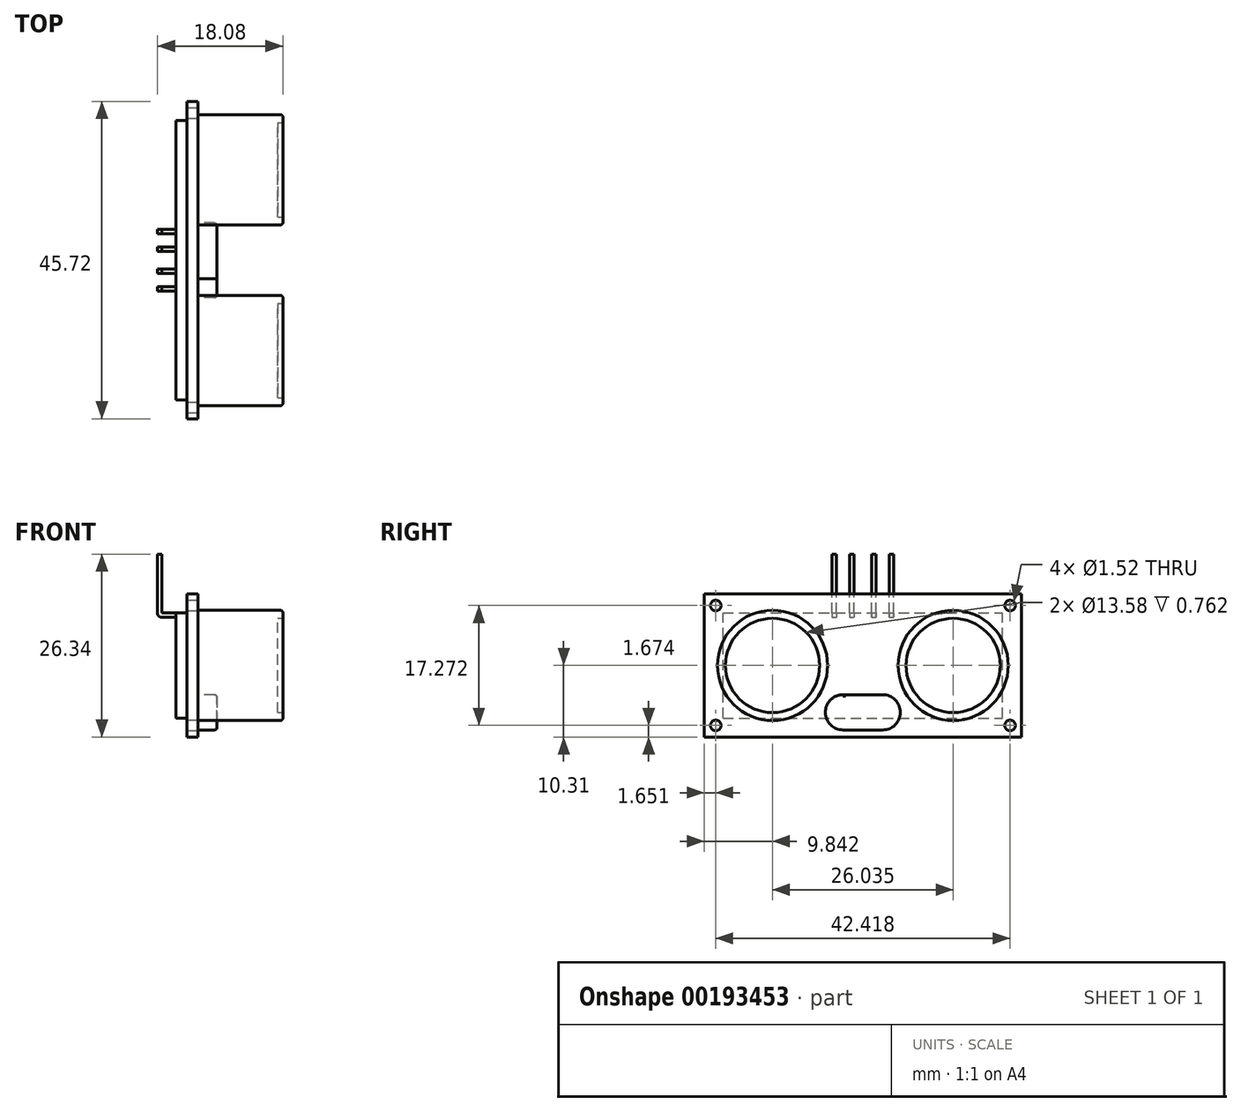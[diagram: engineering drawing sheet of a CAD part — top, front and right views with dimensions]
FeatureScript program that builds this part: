
annotation { "Feature Type Name" : "Feature", "Feature Type Description" : "" }
export const myFeature = defineFeature(function(context is Context, id is Id, definition is map)
    precondition{}
    {
        {
            var Q0;
            Q0=qCreatedBy(makeId("Right.planeOp"),FACE);
            var sketch = newSketch(context, id + "F0", { "sketchPlane" : qUnion([Q0])});
            skLineSegment(sketch, "E0.bottom", {"start": v(22.86, -10.31) * mm, "end": v(-22.86, -10.31) * mm});
            skLineSegment(sketch, "E0.top", {"start": v(22.86, 10.31) * mm, "end": v(-22.86, 10.31) * mm});
            skLineSegment(sketch, "E0.left", {"start": v(22.86, -10.31) * mm, "end": v(22.86, 10.31) * mm});
            skLineSegment(sketch, "E0.right", {"start": v(-22.86, -10.31) * mm, "end": v(-22.86, 10.31) * mm});
            skPoint(sketch, "E0.middle", {"position": v(0, 0) * mm});
            skSolve(sketch);
        }
        {
            var Q0;
            Q0=makeQuery(id+"F0.imprint","IMPRINT",FACE,{"disambiguationData":[TD([[makeQuery(id+"F0.imprint","IMPRINT",EDGE,{"derivedFrom":sQuery(id+"F0.wireOp",EDGE,"E0.bottom")}),-1.0]])]});
            extrude(context, id + "F1", {"entities" : qUnion([Q0]), "oppositeDirection" : true, "depth" : 3.17 * mm});
        }
        {
            var Q0;
            Q0=makeQuery(id+"F1.opExtrude","CAP_FACE",FACE,{"disambiguationData":[OSD([sQuery(id+"F0.wireOp",EDGE,"E0.bottom"),sQuery(id+"F0.wireOp",EDGE,"E0.top"),sQuery(id+"F0.wireOp",EDGE,"E0.left"),sQuery(id+"F0.wireOp",EDGE,"E0.right")])],"isStart":true});
            var sketch = newSketch(context, id + "F2", { "sketchPlane" : qUnion([Q0])});
            skLineSegment(sketch, "E1", {"start": v(0, 0) * mm, "end": v(19.75, 0) * mm, "construction": true});
            skLineSegment(sketch, "E2", {"start": v(0, 0) * mm, "end": v(0, -13.51) * mm, "construction": true});
            skCircle(sketch, "E3", {"center": v(-13.02, 0) * mm, "radius": 7.94 * mm});
            skCircle(sketch, "E4.MirrorC", {"center": v(13.02, 0) * mm, "radius": 7.94 * mm});
            skSolve(sketch);
        }
        {
            var Q0;
            Q0 = qSketchRegion(id + "F2", true);
            extrude(context, id + "F3", {"entities" : qUnion([Q0]), "operationType" : NewBodyOperationType.ADD, "depth" : 12.24 * mm});
        }
        {
            var Q0;
            Q0=makeQuery(id+"F1.opExtrude","CAP_FACE",FACE,{"disambiguationData":[OSD([sQuery(id+"F0.wireOp",EDGE,"E0.bottom"),sQuery(id+"F0.wireOp",EDGE,"E0.top"),sQuery(id+"F0.wireOp",EDGE,"E0.left"),sQuery(id+"F0.wireOp",EDGE,"E0.right")])],"isStart":true});
            var sketch = newSketch(context, id + "F4", { "sketchPlane" : qUnion([Q0])});
            skLineSegment(sketch, "E5", {"start": v(0, 0) * mm, "end": v(0, -8.96) * mm, "construction": true});
            skLineSegment(sketch, "E6", {"start": v(0, 0) * mm, "end": v(11, 0) * mm, "construction": true});
            skCircle(sketch, "E7", {"center": v(-21.2, 8.64) * mm, "radius": 0.76 * mm});
            skCircle(sketch, "E8.MirrorC", {"center": v(21.2, 8.64) * mm, "radius": 0.76 * mm});
            skCircle(sketch, "E9.MirrorC", {"center": v(-21.2, -8.64) * mm, "radius": 0.76 * mm});
            skCircle(sketch, "E10.MirrorC", {"center": v(21.2, -8.64) * mm, "radius": 0.76 * mm});
            skSolve(sketch);
        }
        {
            var Q0;
            Q0 = qSketchRegion(id + "F4", true);
            extrude(context, id + "F5", {"entities" : qUnion([Q0]), "operationType" : NewBodyOperationType.REMOVE, "oppositeDirection" : true, "depth" : 25.4 * mm});
        }
        {
            var Q0;
            Q0=makeQuery(id+"F1.opExtrude","CAP_FACE",FACE,{"disambiguationData":[OSD([sQuery(id+"F0.wireOp",EDGE,"E0.bottom"),sQuery(id+"F0.wireOp",EDGE,"E0.top"),sQuery(id+"F0.wireOp",EDGE,"E0.left"),sQuery(id+"F0.wireOp",EDGE,"E0.right")])],"isStart":false});
            var sketch = newSketch(context, id + "F6", { "sketchPlane" : qUnion([Q0])});
            skLineSegment(sketch, "E11.bottom", {"start": v(20.15, -7.6) * mm, "end": v(-20.15, -7.6) * mm});
            skLineSegment(sketch, "E11.top", {"start": v(20.15, 7.6) * mm, "end": v(-20.15, 7.6) * mm});
            skLineSegment(sketch, "E11.left", {"start": v(20.15, -7.6) * mm, "end": v(20.15, 7.6) * mm});
            skLineSegment(sketch, "E11.right", {"start": v(-20.15, -7.6) * mm, "end": v(-20.15, 7.6) * mm});
            skPoint(sketch, "E11.middle", {"position": v(0, 0) * mm});
            skLineSegment(sketch, "E12.bottom", {"start": v(25.66, -12.83) * mm, "end": v(-25.66, -12.83) * mm});
            skLineSegment(sketch, "E12.top", {"start": v(25.66, 12.83) * mm, "end": v(-25.66, 12.83) * mm});
            skLineSegment(sketch, "E12.left", {"start": v(25.66, -12.83) * mm, "end": v(25.66, 12.83) * mm});
            skLineSegment(sketch, "E12.right", {"start": v(-25.66, -12.83) * mm, "end": v(-25.66, 12.83) * mm});
            skSolve(sketch);
        }
        {
            var Q0;
            Q0=makeQuery(id+"F6.imprint","IMPRINT",FACE,{"disambiguationData":[TD([[makeQuery(id+"F6.imprint","IMPRINT",EDGE,{"derivedFrom":sQuery(id+"F6.wireOp",EDGE,"E11.bottom")}),1.0]])]});
            var Q1;
            Q1=makeQuery(id+"F6.imprint","IMPRINT",FACE,{"disambiguationData":[TD([[makeQuery(id+"F6.imprint","IMPRINT",EDGE,{"derivedFrom":sQuery(id+"F6.wireOp",EDGE,"E12.bottom")}),-1.0]])]});
            extrude(context, id + "F7", {"entities" : qUnion([Q0, Q1]), "operationType" : NewBodyOperationType.REMOVE, "oppositeDirection" : true, "depth" : 1.57 * mm});
        }
        {
            var Q0;
            Q0=makeQuery(id+"F1.opExtrude","CAP_FACE",FACE,{"disambiguationData":[OSD([sQuery(id+"F0.wireOp",EDGE,"E0.bottom"),sQuery(id+"F0.wireOp",EDGE,"E0.top"),sQuery(id+"F0.wireOp",EDGE,"E0.left"),sQuery(id+"F0.wireOp",EDGE,"E0.right")])],"isStart":true});
            var sketch = newSketch(context, id + "F8", { "sketchPlane" : qUnion([Q0])});
            skLineSegment(sketch, "E13.bottom", {"start": v(-2.69, -4.22) * mm, "end": v(2.86, -4.22) * mm});
            skLineSegment(sketch, "E13.top", {"start": v(-2.85, -9.3) * mm, "end": v(2.88, -9.3) * mm});
            skLineSegment(sketch, "E13.left", {"start": v(-5.4, -6.75) * mm, "end": v(-5.4, -6.76) * mm});
            skPoint(sketch, "E13.middle", {"position": v(0, -6.76) * mm});
            skPoint(sketch, "E14.first.point", {"position": v(2.88, -9.3) * mm});
            skPoint(sketch, "E14.second.point", {"position": v(5.4, -6.76) * mm});
            skPoint(sketch, "E14.third.point", {"position": v(3.38, -4.22) * mm});
            skArc(sketch, "E15", {"start": v(-2.69, -4.22) * mm, "mid": v(-5.4, -6.67) * mm, "end": v(-2.85, -9.3) * mm});
            skPoint(sketch, "E15.first.point", {"position": v(-2.85, -9.3) * mm});
            skPoint(sketch, "E15.second.point", {"position": v(-5.4, -6.76) * mm});
            skPoint(sketch, "E15.third.point", {"position": v(-2.69, -4.22) * mm});
            skArc(sketch, "E16", {"start": v(2.86, -9.3) * mm, "mid": v(5.4, -6.76) * mm, "end": v(2.86, -4.22) * mm});
            skPoint(sketch, "E16.first.point", {"position": v(2.86, -9.3) * mm});
            skPoint(sketch, "E16.second.point", {"position": v(2.86, -4.22) * mm});
            skPoint(sketch, "E17.first.point", {"position": v(3.53, -9.3) * mm});
            skPoint(sketch, "E17.second.point", {"position": v(5.4, -5.54) * mm});
            skPoint(sketch, "E17.third.point", {"position": v(4.54, -4.22) * mm});
            skPoint(sketch, "E18.orphan", {"position": v(5.4, -9.3) * mm});
            skPoint(sketch, "E19.orphan", {"position": v(5.4, -4.22) * mm});
            skPoint(sketch, "E20.orphan", {"position": v(-5.4, -4.22) * mm});
            skPoint(sketch, "E21.orphan", {"position": v(-5.4, -9.3) * mm});
            skSolve(sketch);
        }
        {
            var Q0;
            {var subQ3=sQuery(id+"F8.wireOp",EDGE,"E13.bottom");Q0=makeQuery(id+"F8.imprint","IMPRINT",FACE,{"disambiguationData":[TD([[makeQuery(id+"F8.imprint","IMPRINT",EDGE,{"derivedFrom":subQ3}),-1.0]])]});}
            extrude(context, id + "F9", {"entities" : qUnion([Q0]), "operationType" : NewBodyOperationType.ADD, "depth" : 2.74 * mm});
        }
        {
            var Q0;
            Q0=qCreatedBy(makeId("Front.planeOp"),FACE);
            cPlane(context, id + "F10", {"entities" : qUnion([Q0]), "cplaneType" : CPlaneType.OFFSET, "offset" : 1.27 * mm, "width" : 152.4 * mm, "height" : 152.4 * mm});
        }
        {
            var Q0;
            Q0=qCreatedBy(id+"F10.planeOp",FACE);
            var sketch = newSketch(context, id + "F11", { "sketchPlane" : qUnion([Q0])});
            skLineSegment(sketch, "E22", {"start": v(-1.89, 6.96) * mm, "end": v(-5.29, 6.96) * mm});
            skLineSegment(sketch, "E23", {"start": v(-5.84, 7.51) * mm, "end": v(-5.84, 16.03) * mm});
            skPoint(sketch, "E24.visualSharp", {"position": v(-5.84, 6.96) * mm});
            skArc(sketch, "E24.filletArc", {"start": v(-5.84, 7.51) * mm, "mid": v(-5.68, 7.12) * mm, "end": v(-5.29, 6.96) * mm});
            skLineSegment(sketch, "E25.0", {"start": v(-1.89, 7.57) * mm, "end": v(-5.23, 7.57) * mm});
            skLineSegment(sketch, "E26.0", {"start": v(-5.23, 7.57) * mm, "end": v(-5.23, 16.03) * mm});
            skLineSegment(sketch, "E27", {"start": v(-5.84, 16.03) * mm, "end": v(-5.23, 16.03) * mm});
            skLineSegment(sketch, "E28", {"start": v(-1.89, 7.57) * mm, "end": v(-1.89, 6.96) * mm});
            skSolve(sketch);
        }
        {
            var Q0;
            Q0=makeQuery(id+"F11.imprint","IMPRINT",FACE,{"disambiguationData":[TD([[makeQuery(id+"F11.imprint","IMPRINT",EDGE,{"derivedFrom":sQuery(id+"F11.wireOp",EDGE,"E22")}),-1.0]])]});
            extrude(context, id + "F12", {"entities" : qUnion([Q0]), "depth" : 0.64 * mm});
        }
        {
            var Q0;
            Q0=makeQuery(id+"F12.opExtrude","SWEPT_BODY",BODY,{"disambiguationData":[OSD([sQuery(id+"F11.wireOp",EDGE,"E22"),sQuery(id+"F11.wireOp",EDGE,"E23"),sQuery(id+"F11.wireOp",EDGE,"E24.filletArc"),sQuery(id+"F11.wireOp",EDGE,"E25.0"),sQuery(id+"F11.wireOp",EDGE,"E26.0"),sQuery(id+"F11.wireOp",EDGE,"E27"),sQuery(id+"F11.wireOp",EDGE,"E28")])]});
            transform(context, id + "F13", {"entities" : qUnion([Q0]), "transformType" : TransformType.TRANSLATION_3D, "dx" : 0 * mm, "dy" : -2.54 * mm, "dz" : 0 * mm, "makeCopy" : true});
        }
        {
            var Q0;
            Q0=makeQuery(id+"F13.opPattern","COPY",BODY,{"derivedFrom":makeQuery(id+"F12.opExtrude","SWEPT_BODY",BODY,{"disambiguationData":[OSD([sQuery(id+"F11.wireOp",EDGE,"E22"),sQuery(id+"F11.wireOp",EDGE,"E23"),sQuery(id+"F11.wireOp",EDGE,"E24.filletArc"),sQuery(id+"F11.wireOp",EDGE,"E25.0"),sQuery(id+"F11.wireOp",EDGE,"E26.0"),sQuery(id+"F11.wireOp",EDGE,"E27"),sQuery(id+"F11.wireOp",EDGE,"E28")])]}),"instanceName":"1"});
            var Q1;
            Q1=makeQuery(id+"F12.opExtrude","SWEPT_BODY",BODY,{"disambiguationData":[OSD([sQuery(id+"F11.wireOp",EDGE,"E22"),sQuery(id+"F11.wireOp",EDGE,"E23"),sQuery(id+"F11.wireOp",EDGE,"E24.filletArc"),sQuery(id+"F11.wireOp",EDGE,"E25.0"),sQuery(id+"F11.wireOp",EDGE,"E26.0"),sQuery(id+"F11.wireOp",EDGE,"E27"),sQuery(id+"F11.wireOp",EDGE,"E28")])]});
            var Q2;
            Q2=qCreatedBy(makeId("Front.planeOp"),FACE);
            mirror(context, id + "F14", {"operationType" : NewBodyOperationType.ADD, "entities" : qUnion([Q0, Q1]), "mirrorPlane" : qUnion([Q2])});
        }
        {
            var Q0;
            Q0=makeQuery(id+"F9.opExtrude","CAP_EDGE",EDGE,{"disambiguationData":[OSD([sQuery(id+"F8.wireOp",EDGE,"E16")])],"isStart":false});
            var Q1;
            Q1=makeQuery(id+"F3.opExtrude","CAP_EDGE",EDGE,{"disambiguationData":[OSD([sQuery(id+"F2.wireOp",EDGE,"E3")])],"isStart":false});
            var Q2;
            Q2=makeQuery(id+"F3.opExtrude","CAP_EDGE",EDGE,{"disambiguationData":[OSD([sQuery(id+"F2.wireOp",EDGE,"E4.MirrorC")])],"isStart":false});
            fillet(context, id + "F15", {"entities" : qUnion([Q0, Q1, Q2]), "radius" : 0.38 * mm, "tangentPropagation" : true, "allowEdgeOverflow" : false});
        }
        {
            var Q0;
            Q0=makeQuery(id+"F3.opExtrude","CAP_FACE",FACE,{"disambiguationData":[OSD([sQuery(id+"F2.wireOp",EDGE,"E4.MirrorC")])],"isStart":false});
            var sketch = newSketch(context, id + "F16", { "sketchPlane" : qUnion([Q0])});
            skCircle(sketch, "E29", {"center": v(13.02, 0) * mm, "radius": 6.8 * mm});
            skLineSegment(sketch, "E30", {"start": v(0, 0) * mm, "end": v(0, 5.94) * mm, "construction": true});
            skCircle(sketch, "E31.MirrorC", {"center": v(-13.02, 0) * mm, "radius": 6.8 * mm});
            skSolve(sketch);
        }
        {
            var Q0;
            Q0 = qSketchRegion(id + "F16", true);
            extrude(context, id + "F17", {"entities" : qUnion([Q0]), "operationType" : NewBodyOperationType.REMOVE, "oppositeDirection" : true, "depth" : 0.76 * mm});
        }
    });
